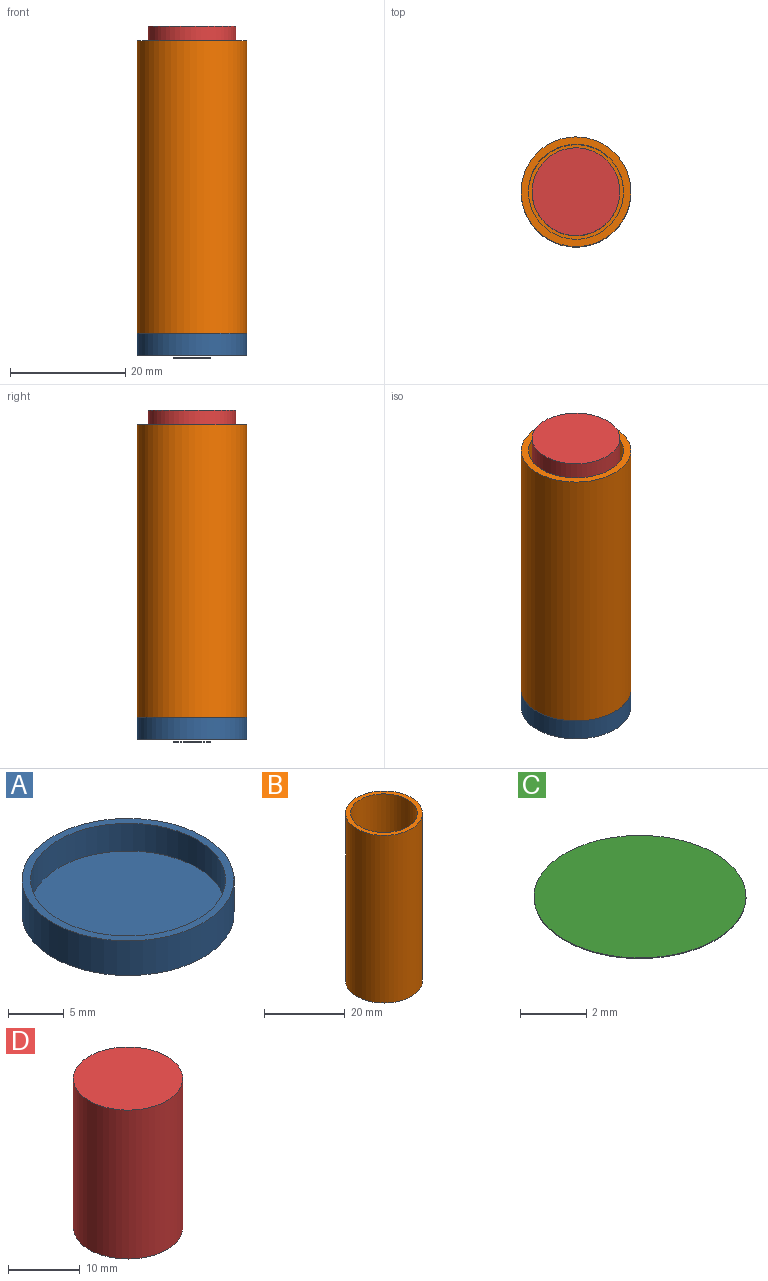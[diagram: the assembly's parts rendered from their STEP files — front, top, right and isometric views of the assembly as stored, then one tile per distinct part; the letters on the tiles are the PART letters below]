
ASSEMBLY  parts=4 mates=3
PART A: 5 faces, bbox 19.1x19.1x3.8 mm
  f0: cylinder r=9.53mm len=19.05mm, axis (0,0,-1), area 228mm2, adj f1,f2
  f1: plane 19.05x19.05mm, normal (0,0,1), area 43.8mm2, adj f0,f3
  f2: plane 19.05x19.05mm, normal (0,0,-1), area 285mm2, adj f0
  f3: cylinder r=8.76mm len=17.53mm, axis (0,0,-1), area 167.8mm2, adj f1,f4
  f4: plane 17.53x17.53mm, normal (0,0,1), area 241.2mm2, adj f3
PART B: 5 faces, bbox 19.1x19.1x50.8 mm
  f0: cylinder r=9.53mm len=50.8mm, axis (0,0,-1), area 3040.2mm2, adj f1,f2
  f1: plane 19.05x19.05mm, normal (0,0,1), area 70.9mm2, adj f0,f3
  f2: plane 19.05x19.05mm, normal (0,0,-1), area 285mm2, adj f0
  f3: cylinder r=8.26mm len=49.53mm, axis (0,0,-1), area 2569mm2, adj f1,f4
  f4: plane 16.51x16.51mm, normal (0,0,1), area 214.1mm2, adj f3
PART C: 3 faces, bbox 6.4x6.4x0 mm
  f0: cylinder r=3.19mm len=6.38mm, axis (0,0,1), area 0.5mm2, adj f1,f2
  f1: plane 6.38x6.38mm, normal (0,0,-1), area 32mm2, adj f0
  f2: plane 6.38x6.38mm, normal (0,0,1), area 32mm2, adj f0
PART D: 3 faces, bbox 15.2x15.2x25.4 mm
  f0: cylinder r=7.62mm len=25.4mm, axis (0,0,-1), area 1216.1mm2, adj f1,f2
  f1: plane 15.24x15.24mm, normal (0,0,1), area 182.4mm2, adj f0
  f2: plane 15.24x15.24mm, normal (0,0,-1), area 182.4mm2, adj f0
PLACE A rot(axis=(-0.08,1,0),180deg) t=(-0.6,13.78,40.98)mm
PLACE B t=(-0.6,13.78,40.98)mm fixed
PLACE C rot(axis=(0,0,1),9deg) t=(-0.6,13.78,36.69)mm
PLACE D t=(-0.6,13.78,68.92)mm
MATE slider D.f0 <-> B.f0  axis (0,0,-1) through (-0.6,13.78,68.92)mm
MATE revolute C.f0 <-> A.f0  axis (0,0,-1) through (-0.6,13.78,36.66)mm
MATE revolute B.f0 <-> A.f0  axis (0,0,-1) through (-0.6,13.78,40.98)mm
